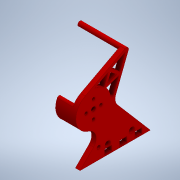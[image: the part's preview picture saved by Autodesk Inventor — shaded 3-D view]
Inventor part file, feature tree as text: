
AUTODESK INVENTOR PART (.ipt)
format: ipt  version: 2020 (Build 240168000, 168)  size: 588,288 bytes
history: native  units: mm
features: extrude x14, sketch x13, other x3, fillet x3, chamfer x1, projected_geometry x1
ambient origin geometry x8: Origin, YZ Plane, XZ Plane, XY Plane, X Axis, Y Axis, Z Axis, Center Point
bodies: Solid1 (feature_tree)
feature tree (35):
  other  "WeaponMountBasePlateV1.ipt"
  extrude  "Extrusion1"  Depth=27.8mm
  extrude  "Extrusion2"  Depth=0.5mm
  extrude  "Extrusion3"  Depth=4.5mm
  extrude  "Extrusion4"  Depth=16.0mm
  fillet  "Fillet1"  Radius=3.1mm
  extrude  "Extrusion5"  Depth=19.0mm
  fillet  "Fillet3"  Radius=3.1mm
  extrude  "Extrusion6"  TaperAngle=0.0deg  [1 undecoded]
  extrude  "Extrusion7"  TaperAngle=0.0deg  [1 undecoded]
  extrude  "Extrusion8"  Depth=17.0mm TaperAngle=0.0deg
  extrude  "Extrusion9"  Depth=2.5mm
  extrude  "Extrusion10"  Depth=7.0mm TaperAngle=0.0deg
  fillet  "Fillet4"  Radius=1.0mm
  extrude  "Extrusion11"  Depth=4.0mm
  chamfer  "Chamfer1"  Distance=9.0mm
  extrude  "Extrusion12"  Depth=2.0mm
  sketch  "Sketch17"  dims[d36=2.0mm d37=2.0mm d39=2.0mm d40=61.487mm d41=0.0mm d43=3.490659mm d45=45.0mm d46=0.0mm d47=2.1mm d48=6.0mm d49=0.0mm d50=6.1mm d51=6.1mm d52=6.0mm d53=-7.853982mm d54=1.0mm d55=8.5mm d56=3.0mm d57=0.0mm d58=1.0mm d59=2.0mm d60=45.0deg d61=10.0mm d62=0.0mm d76=3.0mm d77=3.0mm d78=3.0mm d79=1.5mm d80=1.5mm d81=0.0mm d82=0.0mm d83=10.0mm d84=0.0mm]
  extrude  "Extrusion15"  Depth=2.0mm
  extrude  "Extrusion16"  Depth=10.0mm TaperAngle=0.0deg
  other  "Solid1::WeaponMountBasePlateV1.ipt"
  other  "TaggingFeature1"
  sketch  "Sketch2"  dims[d0=10.0mm d2=27.8mm]
  sketch  "Sketch3"  dims[d3=5.0mm d4=0.5mm]
  sketch  "Sketch4"  dims[d5=17.0mm d6=0.0mm d7=4.5mm]
  sketch  "Sketch6"  dims[d8=17.0mm d9=0.0mm d10=16.0mm d11=3.1mm]
  sketch  "Sketch8"  dims[d12=3.1mm d13=19.0mm d14=3.1mm]
  sketch  "Sketch9"  dims[d15=3.1mm d16=0.0mm d17=0.0mm]
  sketch  "Sketch10"  dims[d18=180.0deg d19=0.0mm]
  projected_geometry  "Projected Loop1"
  sketch  "Sketch11"  dims[d20=4.363323mm d21=17.0mm d22=0.0mm]
  sketch  "Sketch12"  dims[d23=10.0mm d25=2.5mm]
  sketch  "Sketch13"  dims[d27=12.0mm d28=7.0mm d29=0.0mm d30=1.0mm]
  sketch  "Sketch14"  dims[d31=13.0mm d32=4.0mm]
  sketch  "Sketch15"  dims[d33=10.0mm d34=9.0mm d35=0.0mm]
note: 2 required parameter values undecoded (feature->parameter linkage not recoverable at this tier; creation-order binding heuristic only, values carry confidence <= 0.55)
